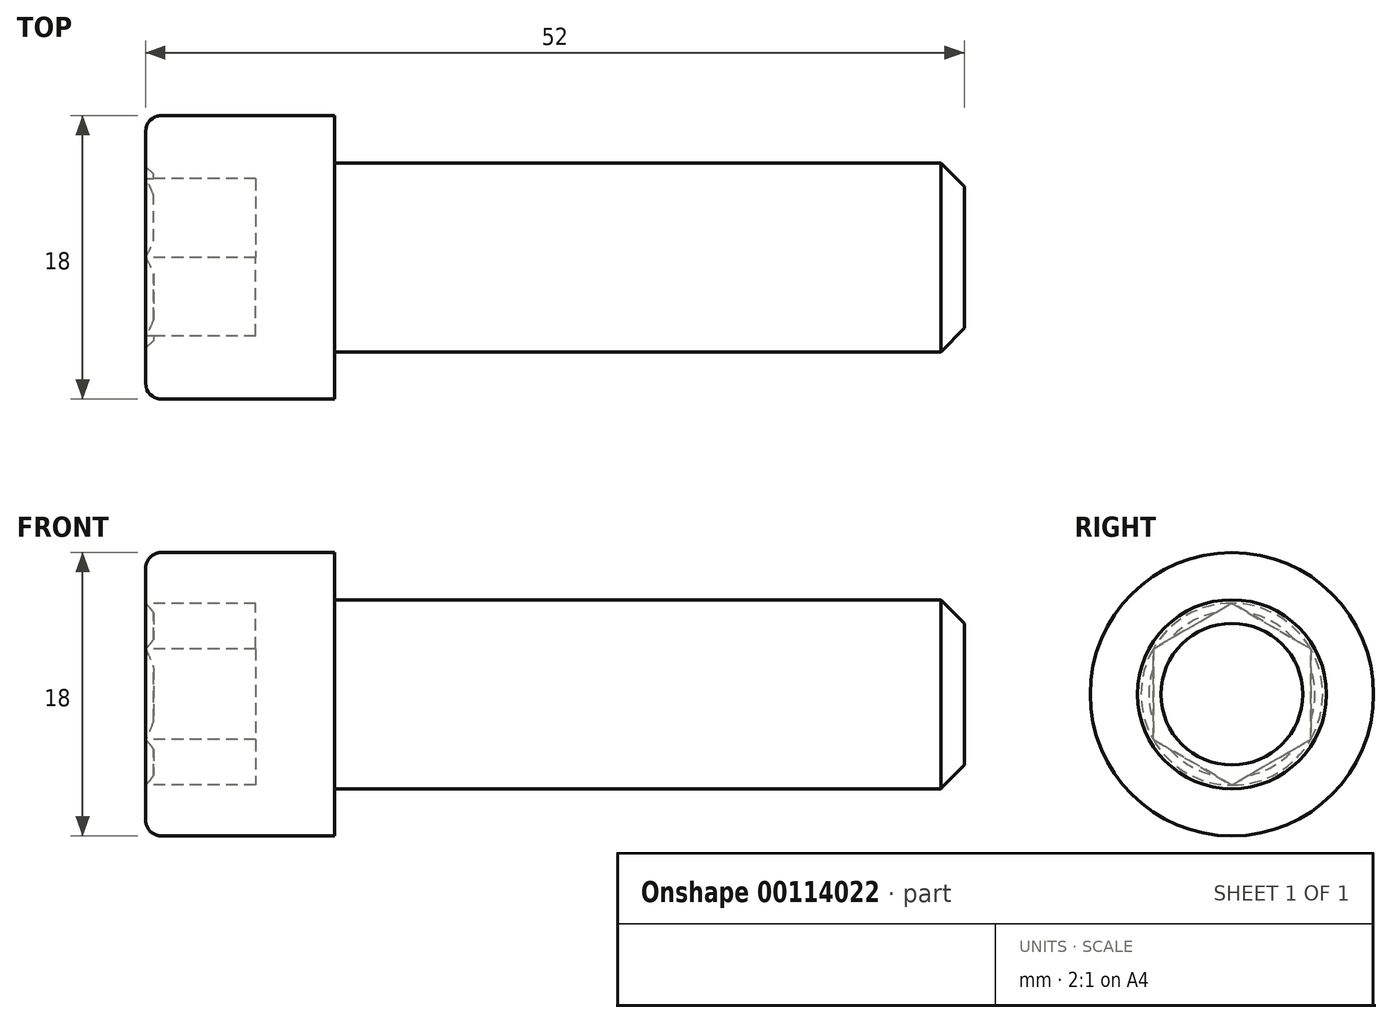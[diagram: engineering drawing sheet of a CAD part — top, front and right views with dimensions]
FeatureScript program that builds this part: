
annotation { "Feature Type Name" : "Feature", "Feature Type Description" : "" }
export const myFeature = defineFeature(function(context is Context, id is Id, definition is map)
    precondition{}
    {
        {
            var Q0;
            Q0=qCreatedBy(makeId("Top.planeOp"),FACE);
            var sketch = newSketch(context, id + "F0", { "sketchPlane" : qUnion([Q0])});
            skLineSegment(sketch, "E0", {"start": v(-38, 0) * mm, "end": v(39.08, 0) * mm, "construction": true});
            skLineSegment(sketch, "E1", {"start": v(-30.75, 0) * mm, "end": v(-30.75, 9) * mm});
            skLineSegment(sketch, "E2", {"start": v(-30.75, 9) * mm, "end": v(-18.75, 9) * mm});
            skLineSegment(sketch, "E3", {"start": v(-18.75, 9) * mm, "end": v(-18.75, 6) * mm});
            skLineSegment(sketch, "E4", {"start": v(-18.75, 6) * mm, "end": v(21.25, 6) * mm});
            skLineSegment(sketch, "E5", {"start": v(21.25, 6) * mm, "end": v(21.25, 0) * mm});
            skLineSegment(sketch, "E6", {"start": v(-30.75, 0) * mm, "end": v(21.25, 0) * mm});
            skSolve(sketch);
        }
        {
            var Q0;
            Q0 = qSketchRegion(id + "F0", true);
            var Q1;
            Q1=sQuery(id+"F0.wireOp",EDGE,"E0");
            revolve(context, id + "F1", {"entities" : qUnion([Q0]), "axis" : qUnion([Q1]), "revolveType" : RevolveType.FULL});
        }
        {
            var Q0;
            Q0=makeQuery(id+"F1.opRevolve","SWEPT_EDGE",EDGE,{"disambiguationData":[OSD([sQuery(id+"F0.wireOp",EDGE,"E1"),sQuery(id+"F0.wireOp",EDGE,"E2")])]});
            fillet(context, id + "F2", {"entities" : qUnion([Q0]), "radius" : 1 * mm, "tangentPropagation" : true, "allowEdgeOverflow" : false});
        }
        {
            var Q0;
            Q0=makeQuery(id+"F1.opRevolve","SWEPT_EDGE",EDGE,{"disambiguationData":[OSD([sQuery(id+"F0.wireOp",EDGE,"E4"),sQuery(id+"F0.wireOp",EDGE,"E5")])]});
            chamfer(context, id + "F3", {"entities" : qUnion([Q0]), "width" : 1.5 * mm, "tangentPropagation" : true});
        }
        {
            var Q0;
            Q0=makeQuery(id+"F1.opRevolve","SWEPT_FACE",FACE,{"disambiguationData":[OSD([sQuery(id+"F0.wireOp",EDGE,"E1")])]});
            var sketch = newSketch(context, id + "F4", { "sketchPlane" : qUnion([Q0])});
            skPoint(sketch, "E7", {"position": v(0, 0) * mm});
            skLineSegment(sketch, "E8", {"start": v(0, 0) * mm, "end": v(0, 4.33) * mm, "construction": true});
            skLineSegment(sketch, "E9", {"start": v(5, 0) * mm, "end": v(5, 2.89) * mm});
            skLineSegment(sketch, "E10", {"start": v(5, 2.89) * mm, "end": v(0, 5.77) * mm});
            skLineSegment(sketch, "E11.MirrorCS", {"start": v(5, -2.89) * mm, "end": v(0, -5.77) * mm});
            skLineSegment(sketch, "E12.MirrorCS", {"start": v(5, 0) * mm, "end": v(5, -2.89) * mm});
            skLineSegment(sketch, "E13.MirrorCS", {"start": v(-5, -2.89) * mm, "end": v(0, -5.77) * mm});
            skLineSegment(sketch, "E14.MirrorCS", {"start": v(-5, 0) * mm, "end": v(-5, -2.89) * mm});
            skLineSegment(sketch, "E15.MirrorCS", {"start": v(-5, 0) * mm, "end": v(-5, 2.89) * mm});
            skLineSegment(sketch, "E16.MirrorCS", {"start": v(-5, 2.89) * mm, "end": v(0, 5.77) * mm});
            skSolve(sketch);
        }
        {
            var Q0;
            Q0=makeQuery(id+"F4.imprint","IMPRINT",FACE,{"disambiguationData":[TD([[makeQuery(id+"F4.imprint","IMPRINT",EDGE,{"derivedFrom":sQuery(id+"F4.wireOp",EDGE,"E9")}),1.0]])]});
            extrude(context, id + "F5", {"entities" : qUnion([Q0]), "operationType" : NewBodyOperationType.REMOVE, "oppositeDirection" : true, "depth" : 7 * mm});
        }
        {
            var Q0;
            Q0=qCreatedBy(makeId("Front.planeOp"),FACE);
            var sketch = newSketch(context, id + "F6", { "sketchPlane" : qUnion([Q0])});
            skLineSegment(sketch, "E17", {"start": v(-30.75, 5.77) * mm, "end": v(-30.25, 5.27) * mm});
            skLineSegment(sketch, "E18", {"start": v(-30.25, 5.27) * mm, "end": v(-30.25, 0) * mm});
            skLineSegment(sketch, "E19", {"start": v(-30.25, 0) * mm, "end": v(-30.75, 0) * mm});
            skLineSegment(sketch, "E20", {"start": v(-30.75, 0) * mm, "end": v(-30.75, 5.77) * mm});
            skSolve(sketch);
        }
        {
            var Q0;
            Q0 = qSketchRegion(id + "F6", true);
            var Q1;
            Q1=sQuery(id+"F0.wireOp",EDGE,"E0");
            revolve(context, id + "F7", {"operationType" : NewBodyOperationType.REMOVE, "entities" : qUnion([Q0]), "axis" : qUnion([Q1]), "revolveType" : RevolveType.FULL, "oppositeDirection" : true});
        }
        {
            var Q0;
            Q0=makeQuery(id+"F1.opRevolve","SWEPT_BODY",BODY,{"disambiguationData":[OSD([sQuery(id+"F0.wireOp",EDGE,"E1"),sQuery(id+"F0.wireOp",EDGE,"E2"),sQuery(id+"F0.wireOp",EDGE,"E3"),sQuery(id+"F0.wireOp",EDGE,"E4"),sQuery(id+"F0.wireOp",EDGE,"E5"),sQuery(id+"F0.wireOp",EDGE,"E6")])]});
            transform(context, id + "F8", {"entities" : qUnion([Q0]), "transformType" : TransformType.TRANSLATION_3D, "dx" : 0 * mm, "dy" : 0 * mm, "dz" : 0 * mm, "makeCopy" : true});
        }
        {
            var Q0;
            Q0=makeQuery(id+"F8.opPattern","COPY",BODY,{"derivedFrom":makeQuery(id+"F1.opRevolve","SWEPT_BODY",BODY,{"disambiguationData":[OSD([sQuery(id+"F0.wireOp",EDGE,"E1"),sQuery(id+"F0.wireOp",EDGE,"E2"),sQuery(id+"F0.wireOp",EDGE,"E3"),sQuery(id+"F0.wireOp",EDGE,"E4"),sQuery(id+"F0.wireOp",EDGE,"E5"),sQuery(id+"F0.wireOp",EDGE,"E6")])]}),"instanceName":"1"});
            deleteBodies(context, id + "F9", {"entities" : qUnion([Q0])});
        }
    });
